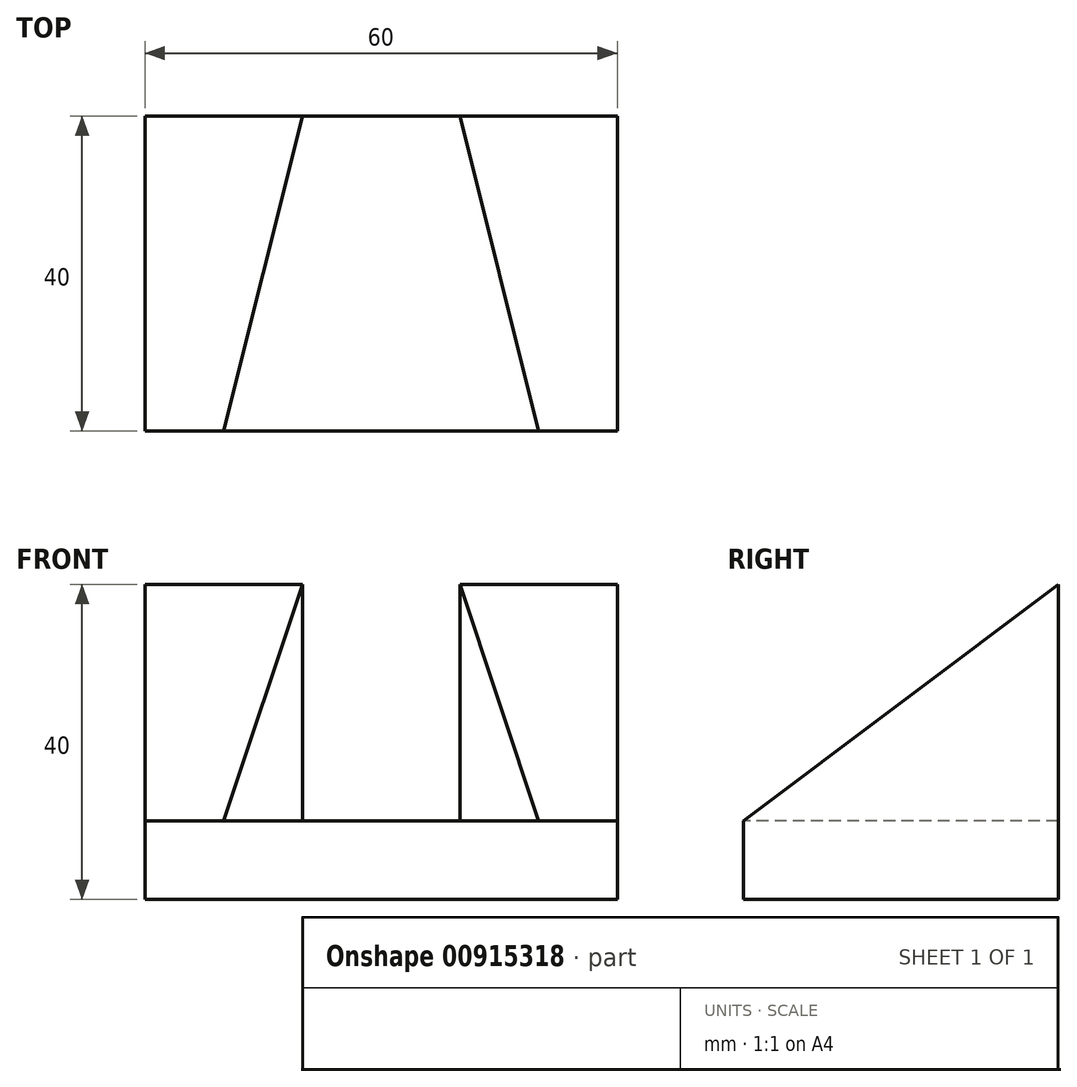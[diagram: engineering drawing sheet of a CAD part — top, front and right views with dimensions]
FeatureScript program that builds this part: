
annotation { "Feature Type Name" : "Feature", "Feature Type Description" : "" }
export const myFeature = defineFeature(function(context is Context, id is Id, definition is map)
    precondition{}
    {
        {
            var Q0;
            Q0=qCreatedBy(makeId("Top.planeOp"),FACE);
            var sketch = newSketch(context, id + "F0", { "sketchPlane" : qUnion([Q0])});
            skLineSegment(sketch, "E0.bottom", {"start": v(0, 0) * mm, "end": v(60, 0) * mm});
            skLineSegment(sketch, "E0.top", {"start": v(0, 40) * mm, "end": v(60, 40) * mm});
            skLineSegment(sketch, "E0.left", {"start": v(0, 0) * mm, "end": v(0, 40) * mm});
            skLineSegment(sketch, "E0.right", {"start": v(60, 0) * mm, "end": v(60, 40) * mm});
            skSolve(sketch);
        }
        {
            var Q0;
            Q0=makeQuery(id+"F0.imprint","IMPRINT",FACE,{"disambiguationData":[TD([[makeQuery(id+"F0.imprint","IMPRINT",EDGE,{"derivedFrom":sQuery(id+"F0.wireOp",EDGE,"E0.bottom")}),1.0]])]});
            extrude(context, id + "F1", {"entities" : qUnion([Q0]), "depth" : 10 * mm, "offsetDistance" : 25 * mm});
        }
        {
            var Q0;
            Q0=makeQuery(id+"F1.opExtrude","CAP_FACE",FACE,{"disambiguationData":[OSD([sQuery(id+"F0.wireOp",EDGE,"E0.bottom"),sQuery(id+"F0.wireOp",EDGE,"E0.top"),sQuery(id+"F0.wireOp",EDGE,"E0.left"),sQuery(id+"F0.wireOp",EDGE,"E0.right")])],"isStart":false});
            var sketch = newSketch(context, id + "F2", { "sketchPlane" : qUnion([Q0])});
            skLineSegment(sketch, "E1.0.0", {"start": v(60, 40) * mm, "end": v(0, 40) * mm});
            skLineSegment(sketch, "E1.0.1", {"start": v(0, 40) * mm, "end": v(0, 0) * mm});
            skLineSegment(sketch, "E1.0.2", {"start": v(0, 0) * mm, "end": v(60, 0) * mm});
            skLineSegment(sketch, "E1.0.3", {"start": v(60, 0) * mm, "end": v(60, 40) * mm});
            skLineSegment(sketch, "E2", {"start": v(10, 0) * mm, "end": v(20, 40) * mm});
            skLineSegment(sketch, "E3", {"start": v(40, 40) * mm, "end": v(50, 0) * mm});
            skLineSegment(sketch, "E4", {"start": v(30, 0) * mm, "end": v(30, 43.9) * mm, "construction": true});
            skSolve(sketch);
        }
        {
            var Q0;
            {var subQ0=sQuery(id+"F2.wireOp",EDGE,"E1.0.1");Q0=makeQuery(id+"F2.imprint","IMPRINT",FACE,{"disambiguationData":[TD([[makeQuery(id+"F2.imprint","IMPRINT",EDGE,{"derivedFrom":subQ0}),-1.0]])]});}
            var Q1;
            {var subQ0=sQuery(id+"F2.wireOp",EDGE,"E1.0.3");Q1=makeQuery(id+"F2.imprint","IMPRINT",FACE,{"disambiguationData":[TD([[makeQuery(id+"F2.imprint","IMPRINT",EDGE,{"derivedFrom":subQ0}),1.0]])]});}
            extrude(context, id + "F3", {"entities" : qUnion([Q0, Q1]), "operationType" : NewBodyOperationType.ADD, "depth" : 30 * mm, "offsetDistance" : 25 * mm});
        }
        {
            var Q0;
            Q0=makeQuery(id+"F3.boolean.opBoolean","MERGE",FACE,{"derivedFrom":[makeQuery(id+"F1.opExtrude","SWEPT_FACE",FACE,{"disambiguationData":[OSD([sQuery(id+"F0.wireOp",EDGE,"E0.right")])]}),makeQuery(id+"F3.opExtrude","SWEPT_FACE",FACE,{"disambiguationData":[OSD([sQuery(id+"F2.wireOp",EDGE,"E1.0.3")])]})]});
            var sketch = newSketch(context, id + "F4", { "sketchPlane" : qUnion([Q0])});
            skLineSegment(sketch, "E5", {"start": v(0, 10) * mm, "end": v(40, 10) * mm, "construction": true});
            skLineSegment(sketch, "E6.0.0", {"start": v(0, 0) * mm, "end": v(40, 0) * mm});
            skLineSegment(sketch, "E6.0.1", {"start": v(40, 0) * mm, "end": v(40, 40) * mm});
            skLineSegment(sketch, "E6.0.2", {"start": v(40, 40) * mm, "end": v(0, 40) * mm});
            skLineSegment(sketch, "E6.0.3", {"start": v(0, 40) * mm, "end": v(0, 0) * mm});
            skLineSegment(sketch, "E7", {"start": v(0, 10) * mm, "end": v(40, 40) * mm});
            skSolve(sketch);
        }
        {
            var Q0;
            {var subQ0=sQuery(id+"F4.wireOp",EDGE,"E6.0.2");Q0=makeQuery(id+"F4.imprint","IMPRINT",FACE,{"disambiguationData":[TD([[makeQuery(id+"F4.imprint","IMPRINT",EDGE,{"derivedFrom":subQ0}),-1.0]])]});}
            extrude(context, id + "F5", {"entities" : qUnion([Q0]), "operationType" : NewBodyOperationType.REMOVE, "endBound" : BoundingType.THROUGH_ALL, "oppositeDirection" : true, "depth" : 25 * mm, "offsetDistance" : 25 * mm});
        }
    });
